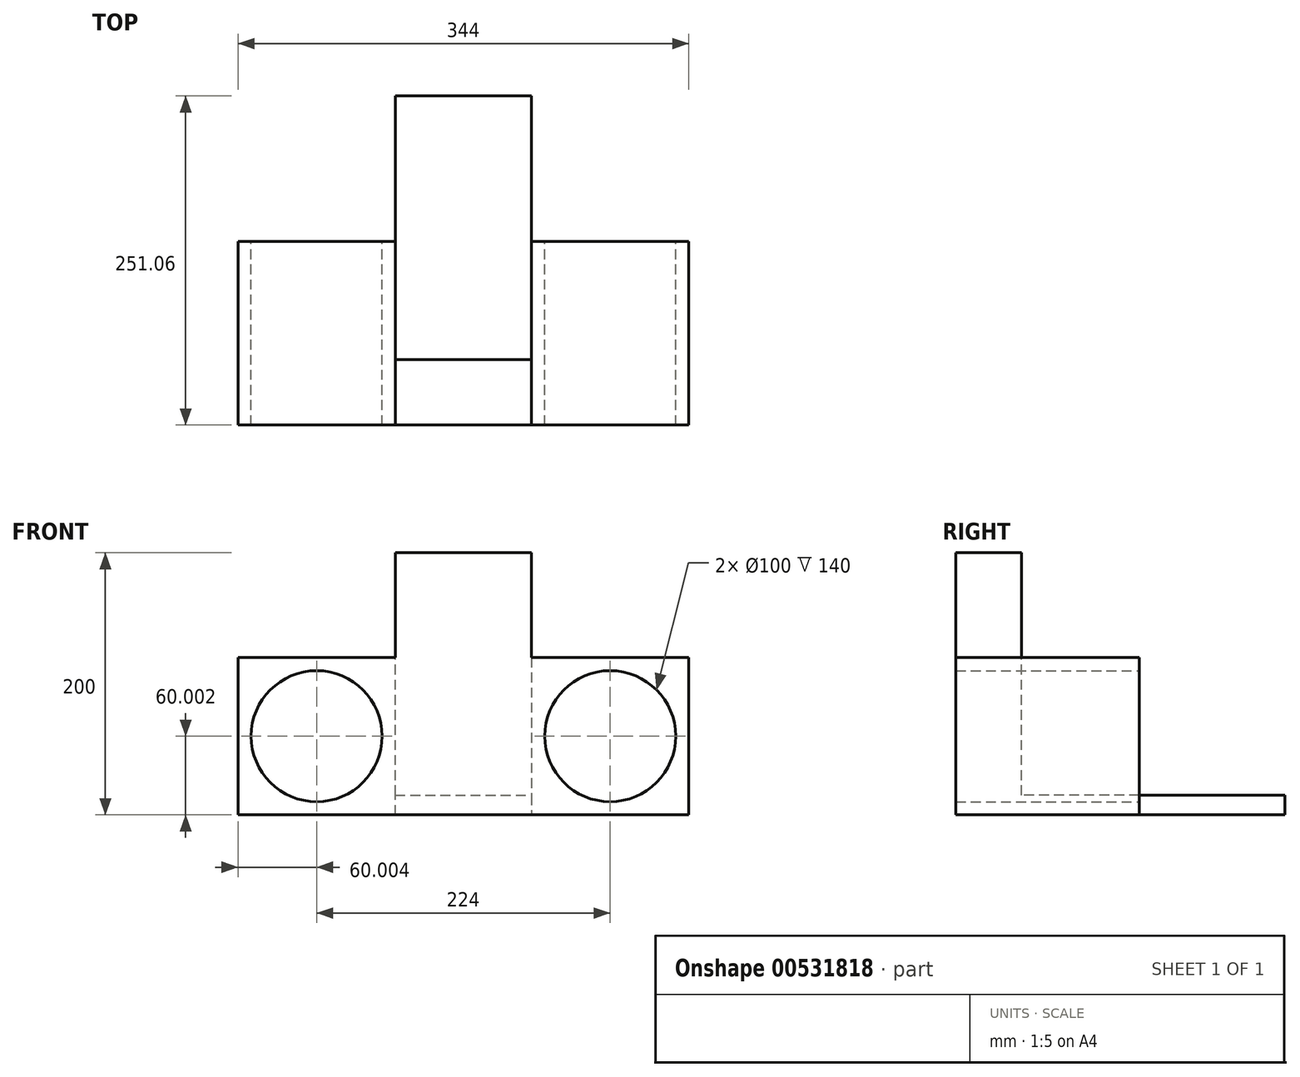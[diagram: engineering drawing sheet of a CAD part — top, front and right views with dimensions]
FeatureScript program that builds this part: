
annotation { "Feature Type Name" : "Feature", "Feature Type Description" : "" }
export const myFeature = defineFeature(function(context is Context, id is Id, definition is map)
    precondition{}
    {
        {
            var Q0;
            Q0=qCreatedBy(makeId("Front.planeOp"),FACE);
            var sketch = newSketch(context, id + "F0", { "sketchPlane" : qUnion([Q0])});
            skLineSegment(sketch, "E0", {"start": v(-99.46, -75.97) * mm, "end": v(-99.46, 124.03) * mm});
            skLineSegment(sketch, "E1", {"start": v(-99.46, 124.03) * mm, "end": v(4.54, 124.03) * mm});
            skLineSegment(sketch, "E2", {"start": v(4.54, 124.03) * mm, "end": v(4.54, -75.97) * mm});
            skLineSegment(sketch, "E3", {"start": v(-99.46, -75.97) * mm, "end": v(4.54, -75.97) * mm});
            skSolve(sketch);
        }
        {
            var Q0;
            Q0=makeQuery(id+"F0.imprint","IMPRINT",FACE,{"disambiguationData":[TD([[makeQuery(id+"F0.imprint","IMPRINT",EDGE,{"derivedFrom":sQuery(id+"F0.wireOp",EDGE,"E0")}),-1.0]])]});
            extrude(context, id + "F1", {"entities" : qUnion([Q0]), "depth" : 50 * mm, "offsetDistance" : 25 * mm});
        }
        {
            var Q0;
            Q0=makeQuery(id+"F1.opExtrude","CAP_FACE",FACE,{"disambiguationData":[OSD([sQuery(id+"F0.wireOp",EDGE,"E0"),sQuery(id+"F0.wireOp",EDGE,"E1"),sQuery(id+"F0.wireOp",EDGE,"E2"),sQuery(id+"F0.wireOp",EDGE,"E3")])],"isStart":false});
            var sketch = newSketch(context, id + "F2", { "sketchPlane" : qUnion([Q0])});
            skLineSegment(sketch, "E4", {"start": v(-99.46, 44.03) * mm, "end": v(-219.46, 44.03) * mm});
            skLineSegment(sketch, "E5", {"start": v(-219.46, 44.03) * mm, "end": v(-219.46, -75.97) * mm});
            skLineSegment(sketch, "E6", {"start": v(-219.46, -75.97) * mm, "end": v(-99.46, -75.97) * mm});
            skLineSegment(sketch, "E7", {"start": v(4.54, 44.03) * mm, "end": v(124.54, 44.03) * mm});
            skLineSegment(sketch, "E8", {"start": v(124.54, 44.03) * mm, "end": v(124.54, -75.97) * mm});
            skLineSegment(sketch, "E9", {"start": v(124.54, -75.97) * mm, "end": v(4.54, -75.97) * mm});
            skSolve(sketch);
        }
        {
            var Q0;
            {var subQ0=sQuery(id+"F2.wireOp",EDGE,"E4");Q0=makeQuery(id+"F2.imprint","IMPRINT",FACE,{"disambiguationData":[TD([[makeQuery(id+"F2.imprint","IMPRINT",EDGE,{"derivedFrom":subQ0}),1.0]])]});}
            var Q1;
            {var subQ0=sQuery(id+"F2.wireOp",EDGE,"E7");Q1=makeQuery(id+"F2.imprint","IMPRINT",FACE,{"disambiguationData":[TD([[makeQuery(id+"F2.imprint","IMPRINT",EDGE,{"derivedFrom":subQ0}),-1.0]])]});}
            extrude(context, id + "F3", {"entities" : qUnion([Q0, Q1]), "operationType" : NewBodyOperationType.ADD, "oppositeDirection" : true, "depth" : 140 * mm, "offsetDistance" : 25 * mm});
        }
        {
            var Q0;
            Q0=makeQuery(id+"F3.opExtrude","CAP_FACE",FACE,{"disambiguationData":[OSD([sQuery(id+"F0.wireOp",EDGE,"E2"),sQuery(id+"F2.wireOp",EDGE,"E7"),sQuery(id+"F2.wireOp",EDGE,"E8"),sQuery(id+"F2.wireOp",EDGE,"E9")])],"isStart":false});
            var sketch = newSketch(context, id + "F4", { "sketchPlane" : qUnion([Q0])});
            skPoint(sketch, "E10.centerSnap0", {"position": v(-4.54, -15.97) * mm});
            skCircle(sketch, "E11", {"center": v(-64.54, -15.97) * mm, "radius": 50 * mm});
            skCircle(sketch, "E12", {"center": v(159.46, -15.97) * mm, "radius": 50 * mm});
            skSolve(sketch);
        }
        {
            var Q0;
            Q0=makeQuery(id+"F4.imprint","IMPRINT",FACE,{"disambiguationData":[TD([[makeQuery(id+"F4.imprint","IMPRINT",EDGE,{"derivedFrom":sQuery(id+"F4.wireOp",EDGE,"E11")}),1.0]])]});
            var Q1;
            Q1=makeQuery(id+"F4.imprint","IMPRINT",FACE,{"disambiguationData":[TD([[makeQuery(id+"F4.imprint","IMPRINT",EDGE,{"derivedFrom":sQuery(id+"F4.wireOp",EDGE,"E12")}),1.0]])]});
            extrude(context, id + "F5", {"entities" : qUnion([Q0, Q1]), "operationType" : NewBodyOperationType.REMOVE, "endBound" : BoundingType.THROUGH_ALL, "oppositeDirection" : true, "depth" : 25 * mm, "offsetDistance" : 25 * mm});
        }
        {
            var Q0;
            Q0=makeQuery(id+"F3.boolean.opBoolean","MERGE",FACE,{"derivedFrom":[makeQuery(id+"F1.opExtrude","SWEPT_FACE",FACE,{"disambiguationData":[OSD([sQuery(id+"F0.wireOp",EDGE,"E3")])]}),makeQuery(id+"F3.opExtrude","SWEPT_FACE",FACE,{"disambiguationData":[OSD([sQuery(id+"F2.wireOp",EDGE,"E6")])]}),makeQuery(id+"F3.opExtrude","SWEPT_FACE",FACE,{"disambiguationData":[OSD([sQuery(id+"F2.wireOp",EDGE,"E9")])]})]});
            var sketch = newSketch(context, id + "F6", { "sketchPlane" : qUnion([Q0])});
            skLineSegment(sketch, "E13.bottom", {"start": v(-99.46, 0) * mm, "end": v(0, 0) * mm});
            skLineSegment(sketch, "E13.top", {"start": v(-99.46, 0) * mm, "end": v(0, 0) * mm});
            skLineSegment(sketch, "E13.left", {"start": v(-99.46, 0) * mm, "end": v(-99.46, 0) * mm});
            skLineSegment(sketch, "E13.right", {"start": v(0, 0) * mm, "end": v(0, 0) * mm});
            skLineSegment(sketch, "E14.bottom", {"start": v(4.54, 0) * mm, "end": v(-99.46, 0) * mm});
            skLineSegment(sketch, "E14.top", {"start": v(4.54, -201.06) * mm, "end": v(-99.46, -201.06) * mm});
            skLineSegment(sketch, "E14.left", {"start": v(4.54, 0) * mm, "end": v(4.54, -201.06) * mm});
            skLineSegment(sketch, "E14.right", {"start": v(-99.46, 0) * mm, "end": v(-99.46, -201.06) * mm});
            skSolve(sketch);
        }
        {
            var Q0;
            {var subQ4=sQuery(id+"F6.wireOp",EDGE,"E14.top");Q0=makeQuery(id+"F6.imprint","IMPRINT",FACE,{"disambiguationData":[TD([[makeQuery(id+"F6.imprint","IMPRINT",EDGE,{"derivedFrom":subQ4}),-1.0]])]});}
            extrude(context, id + "F7", {"entities" : qUnion([Q0]), "operationType" : NewBodyOperationType.ADD, "oppositeDirection" : true, "depth" : 15 * mm, "offsetDistance" : 25 * mm});
        }
    });
